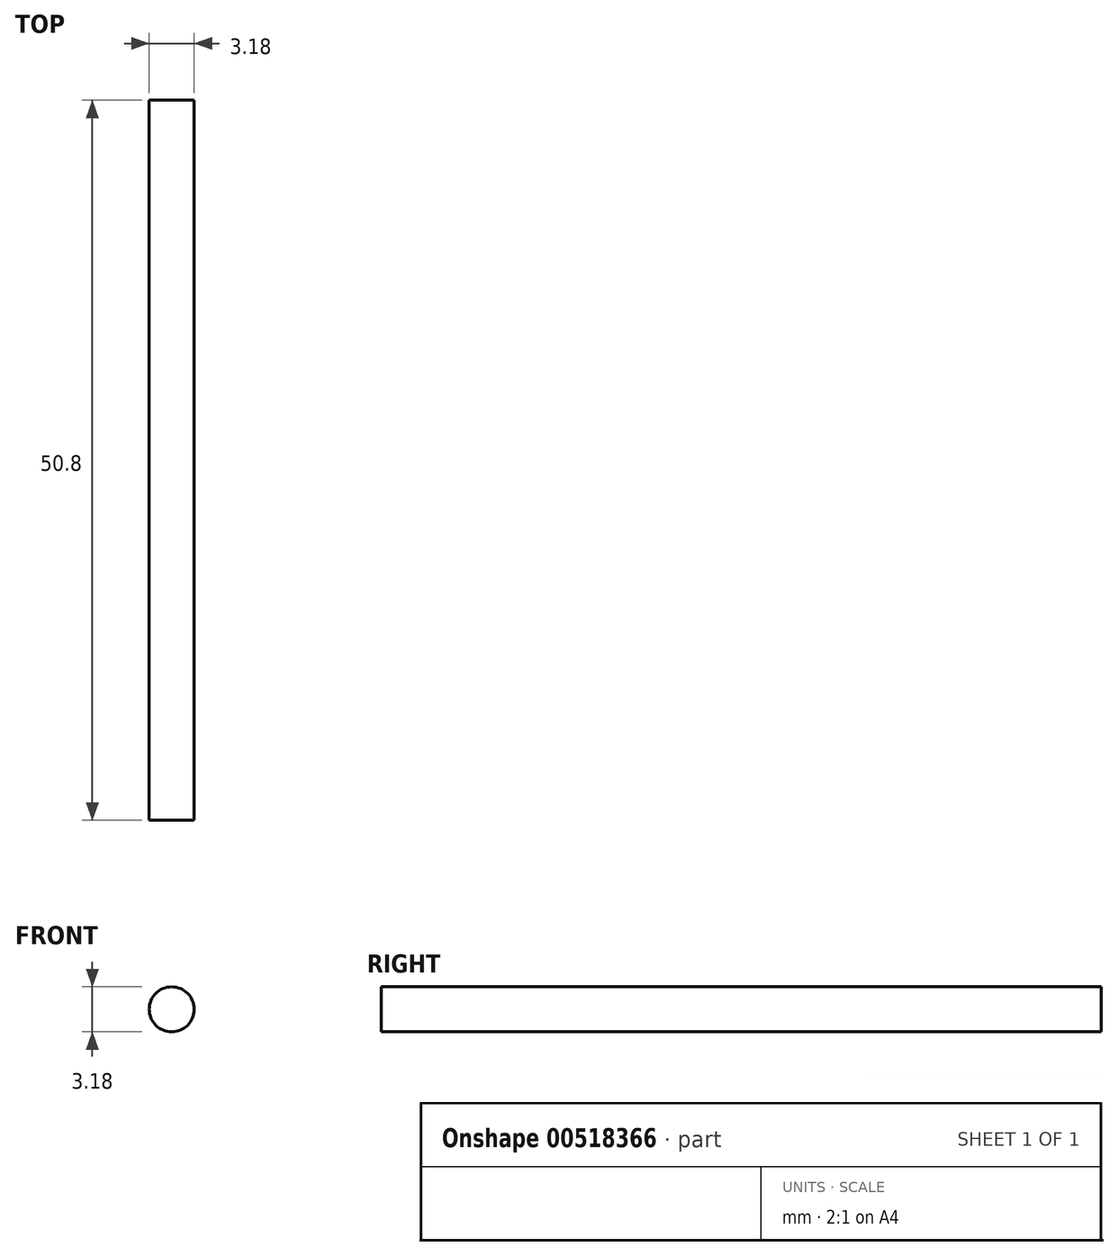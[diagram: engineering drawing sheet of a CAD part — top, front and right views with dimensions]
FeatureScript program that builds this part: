
annotation { "Feature Type Name" : "Feature", "Feature Type Description" : "" }
export const myFeature = defineFeature(function(context is Context, id is Id, definition is map)
    precondition{}
    {
        {
            var Q0;
            Q0=qCreatedBy(makeId("Front.planeOp"),FACE);
            var sketch = newSketch(context, id + "F0", { "sketchPlane" : qUnion([Q0])});
            skCircle(sketch, "E0", {"center": v(0, 0) * mm, "radius": 1.59 * mm});
            skSolve(sketch);
        }
        {
            var Q0;
            Q0 = qSketchRegion(id + "F0", true);
            extrude(context, id + "F1", {"entities" : qUnion([Q0]), "depth" : 50.8 * mm, "offsetDistance" : 25.4 * mm});
        }
    });
